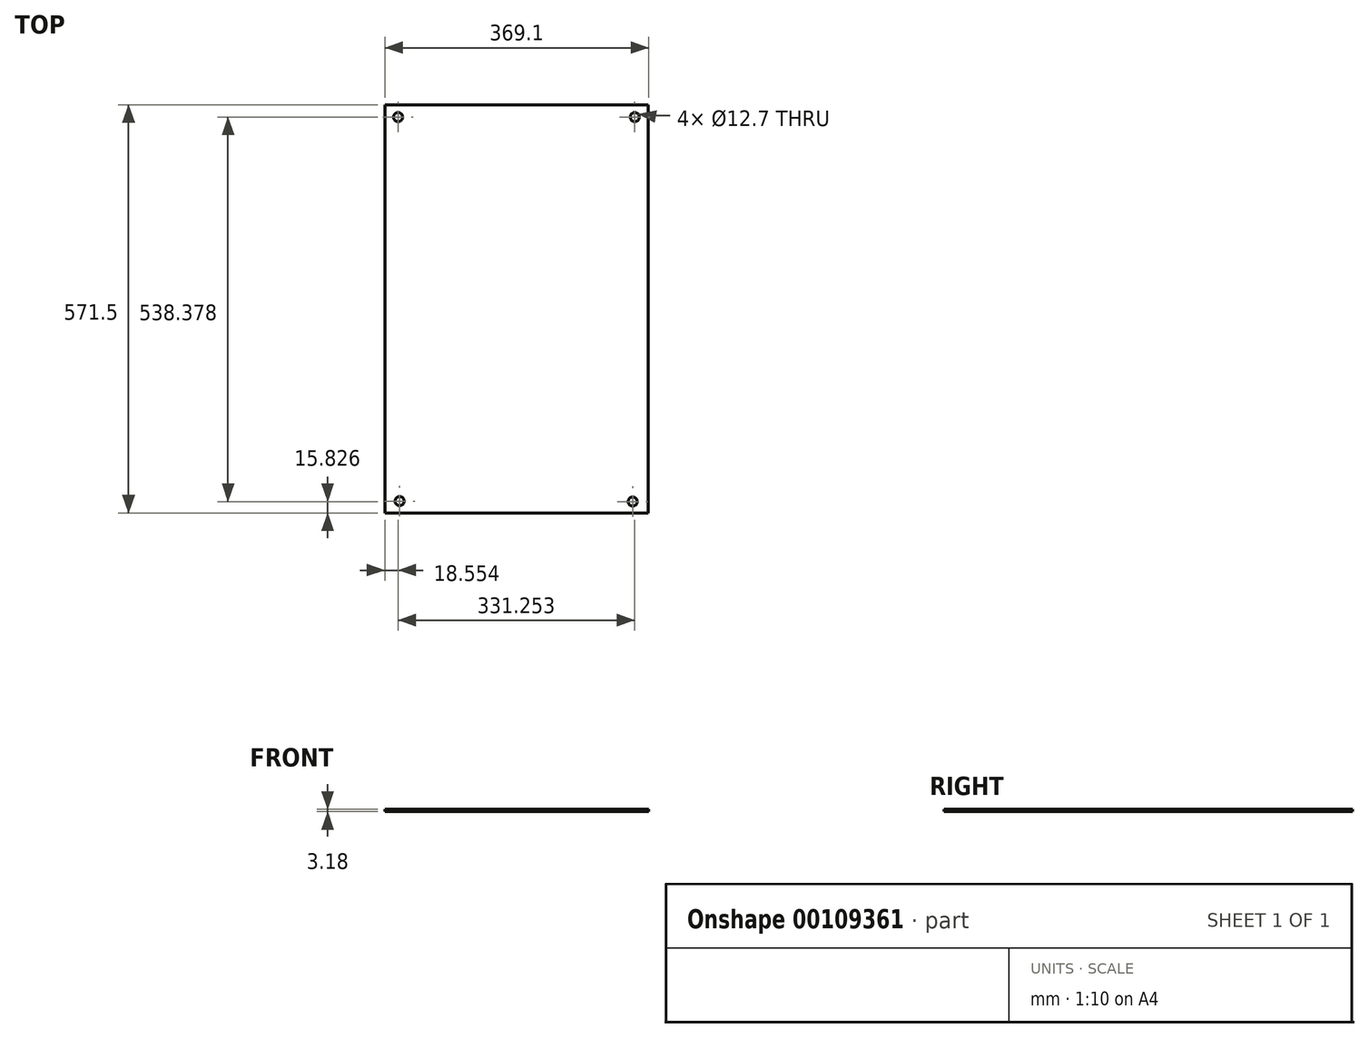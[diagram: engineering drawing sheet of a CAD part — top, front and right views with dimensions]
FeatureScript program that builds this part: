
annotation { "Feature Type Name" : "Feature", "Feature Type Description" : "" }
export const myFeature = defineFeature(function(context is Context, id is Id, definition is map)
    precondition{}
    {
        {
            var Q0;
            Q0=qCreatedBy(makeId("Top.planeOp"),FACE);
            var sketch = newSketch(context, id + "F0", { "sketchPlane" : qUnion([Q0])});
            skLineSegment(sketch, "E0.bottom", {"start": v(184.15, 285.75) * mm, "end": v(-184.15, 285.75) * mm});
            skLineSegment(sketch, "E0.top", {"start": v(184.15, -285.75) * mm, "end": v(-184.15, -285.75) * mm});
            skLineSegment(sketch, "E0.left", {"start": v(184.15, 285.75) * mm, "end": v(184.15, -285.75) * mm});
            skLineSegment(sketch, "E0.right", {"start": v(-184.15, 285.75) * mm, "end": v(-184.15, -285.75) * mm});
            skPoint(sketch, "E0.middle", {"position": v(0, 0) * mm});
            skLineSegment(sketch, "E1.bottom", {"start": v(184.95, -16.37) * mm, "end": v(183.35, -16.37) * mm});
            skLineSegment(sketch, "E1.top", {"start": v(184.95, -16) * mm, "end": v(183.35, -16) * mm});
            skLineSegment(sketch, "E1.left", {"start": v(184.95, -16.37) * mm, "end": v(184.95, -16) * mm});
            skLineSegment(sketch, "E1.right", {"start": v(183.35, -16.37) * mm, "end": v(183.35, -16) * mm});
            skPoint(sketch, "E1.middle", {"position": v(184.15, -16.18) * mm});
            skSolve(sketch);
        }
        {
            var Q0;
            Q0 = qSketchRegion(id + "F0", true);
            extrude(context, id + "F1", {"entities" : qUnion([Q0]), "depth" : 3.17 * mm});
        }
        {
            var Q0;
            Q0=makeQuery(id+"F1.opExtrude","CAP_FACE",FACE,{"disambiguationData":[OSD([sQuery(id+"F0.wireOp",EDGE,"E0.bottom"),sQuery(id+"F0.wireOp",EDGE,"E0.top"),sQuery(id+"F0.wireOp",EDGE,"E0.left"),sQuery(id+"F0.wireOp",EDGE,"E0.right"),sQuery(id+"F0.wireOp",EDGE,"E1.bottom"),sQuery(id+"F0.wireOp",EDGE,"E1.top"),sQuery(id+"F0.wireOp",EDGE,"E1.left")])],"isStart":false});
            var sketch = newSketch(context, id + "F2", { "sketchPlane" : qUnion([Q0])});
            skCircle(sketch, "E2", {"center": v(-165.6, 268.45) * mm, "radius": 6.35 * mm});
            skCircle(sketch, "E3", {"center": v(165.66, 268.45) * mm, "radius": 6.35 * mm});
            skCircle(sketch, "E4", {"center": v(-163.4, -269.19) * mm, "radius": 6.35 * mm});
            skCircle(sketch, "E5", {"center": v(162.72, -269.92) * mm, "radius": 6.35 * mm});
            skSolve(sketch);
        }
        {
            var Q0;
            Q0 = qSketchRegion(id + "F2", true);
            extrude(context, id + "F3", {"entities" : qUnion([Q0]), "operationType" : NewBodyOperationType.REMOVE, "oppositeDirection" : true, "depth" : 3.17 * mm});
        }
    });
